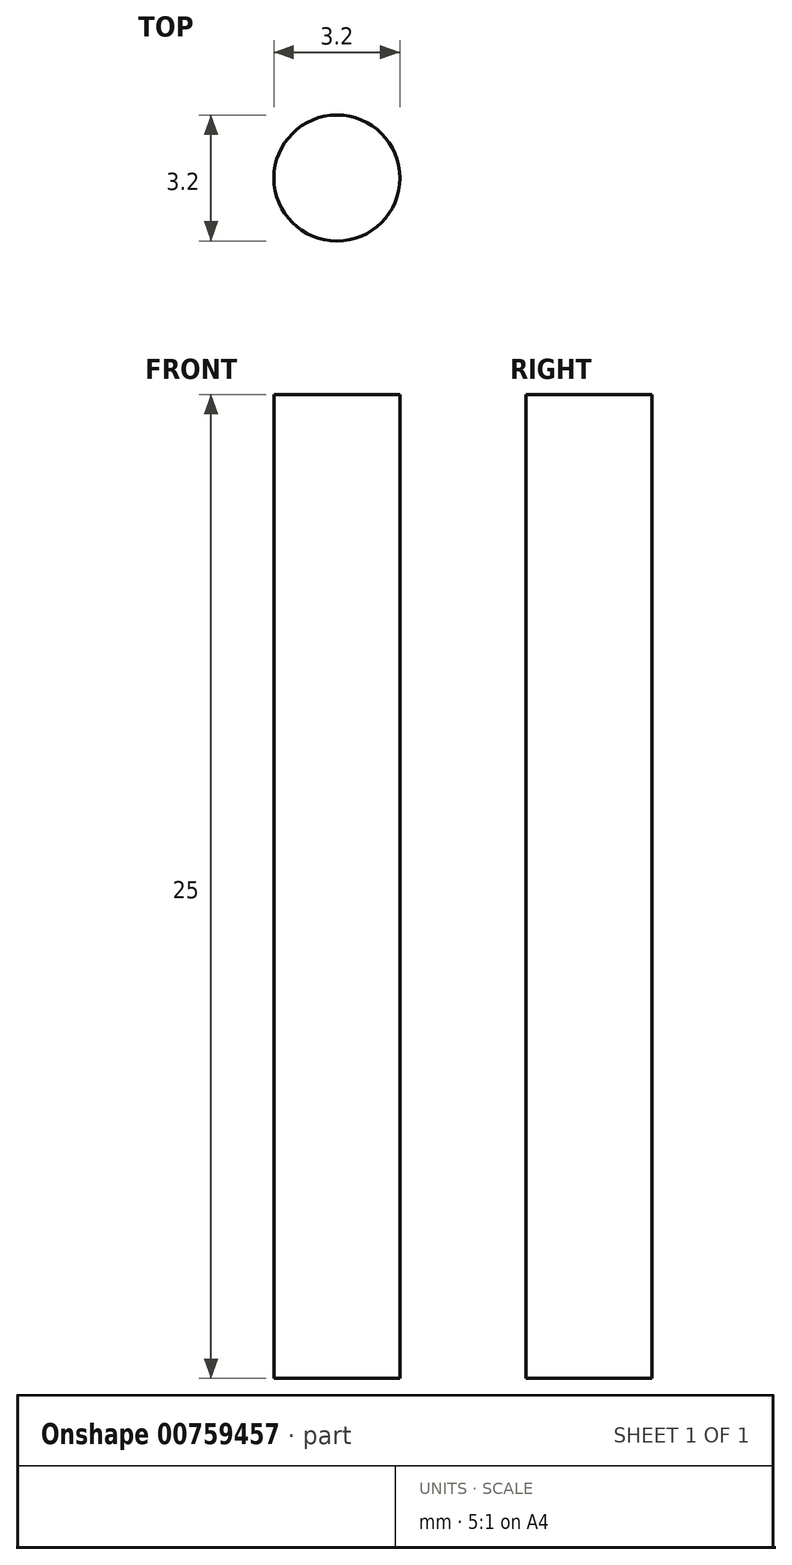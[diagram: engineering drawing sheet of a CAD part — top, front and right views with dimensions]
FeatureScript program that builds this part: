
annotation { "Feature Type Name" : "Feature", "Feature Type Description" : "" }
export const myFeature = defineFeature(function(context is Context, id is Id, definition is map)
    precondition{}
    {
        {
            var Q0;
            Q0=qCreatedBy(makeId("Top.planeOp"),FACE);
            var sketch = newSketch(context, id + "F0", { "sketchPlane" : qUnion([Q0])});
            skCircle(sketch, "E0", {"center": v(0, 0) * mm, "radius": 1.6 * mm});
            skSolve(sketch);
        }
        {
            var Q0;
            Q0=makeQuery(id+"F0.imprint","IMPRINT",FACE,{"disambiguationData":[TD([[makeQuery(id+"F0.imprint","IMPRINT",EDGE,{"derivedFrom":sQuery(id+"F0.wireOp",EDGE,"E0")}),1.0]])]});
            extrude(context, id + "F1", {"entities" : qUnion([Q0]), "oppositeDirection" : true, "depth" : 25 * mm, "offsetDistance" : 25 * mm});
        }
    });
